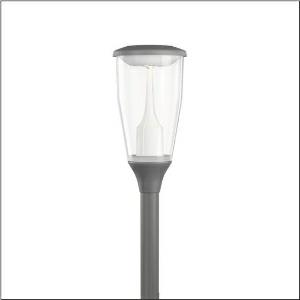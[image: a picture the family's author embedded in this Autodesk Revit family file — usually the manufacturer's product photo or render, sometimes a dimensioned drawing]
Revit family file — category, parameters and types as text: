
# Revit family: dl_11_iq___p1_0a_5xa5565nf14hp00022_fef3
name_source: partatom
category: Lighting Fixtures
units: mm (PartAtom-declared; Revit-internal decimal feet)

## family parameters
Cut with Voids When Loaded = No
Host = Face
Light Source = No
Part Type = Normal
Room Calculation Point = No
Round Connector Dimension = Use Diameter
Shared = No

## types (1)
- --- (1 x LED, 4280 lm, 33.6 W, 2700K)
    Apparent Load = 34 VA
    CIE Flux Codes = 33 63 91 94 100
    Color Rendering = 70
    Color Temperature = 2700K
    Default Elevation = 1800 mm
    Description = DL 11 iQ, mast luminaire, Module 540 iQ-SR, primary light control with 3 zone facetted reflector, of plastic, silver coated, highly specular, structured, primary optical cover: cover, of PMMA, transparent, light distribution: P1.0a, light emission: direct distribution, primary light characteristic: asymmetric, installation type: post-top, LED, High Power LED, light colour: 727, colour temperature: 2700K, control gear: iQ Street-Remote, control: Street-Remote, Auto-Match, Temp-Guard, Lumen-Switch, Night-Set, Smart-Wire, Light-Fading, Desk-Remote (wireless, voltage-free reading and setting of iQ features in the workshop via application-optimized NFC function/RFID function), optimised constant luminous flux control (CLO 2.0), mains connection: 220..240V, AC, 50/60Hz, connection cable pre-assembled, cable length: 5,5m, start of lifetime: 34W, end of service life: 36W, luminaire housing, upper part, of diecast aluminium, coated, SITECO metallic grey (DB 702S), spigot size: 60mm (post-top), mounting height: 3..5m, post-top mast mounting element, of diecast aluminium, coated, SITECO metallic grey (DB 702S), Module 540 iQ-SR, traffic white (RAL 9016), equipment: Power, protection rating (complete): IP66, insulation class (complete): insulation class II (safety insulation), certification: CE, ENEC, ENEC+, VDE, impact resistance: IK07, packaging unit: 1 piece

Light Distribution: P1.0a
    Height = 665 mm
    Lamp = 1 x LED
    Lamp Light Flux = 4280 lm
    Lamp Power = 33.6 W
    Lamp count = 1
    Length = 334 mm
    Luminous efficacy = 127 lm/W
    Manufacturer = Siteco
    ModVariant = No
    Model = 5XA5565NF14HP00022
    Number of Poles = 1
    OnlyDefault = Yes
    Power Factor = 1
    Product Name = DL 11 iQ | P1.0a
    Product group = mast luminaire | pylon top
    ProductGroupID = 6100
    Protection Class = Protection class II
    Protection Degree = IP 66
    RLX_Detail_Level = 1
    RLX_Emergency_Light_Flux = 0 lm
    RLX_Emergency_Type = 0
    RLX_Emergency_Type_DB = No
    RlxData = <blob elided: 104965 chars, md5=733351b8>
    Socket = socket
    Standby Power = 0 W
    System Light Flux = 4280 lm
    System Power = 34 W
    Type Comments = factory setting: luminous flux: 100 % | dim-lin: 254 | 695 mA
    Type Image = l_1258354.jpg
    URL = http://relux.com
    VarID = @adj_039931
    Voltage = 0 V
    Weight = 0.00 kg
    Width = 0 mm  [stored 0 ft]

note: [stored X ft] marks values corroborated as IEEE doubles in the binary element streams (Revit-internal decimal feet)

## geometry (parser evidence)
native form markers: Blend x4, Sweep x10
no freeform markers — native parametric forms only
